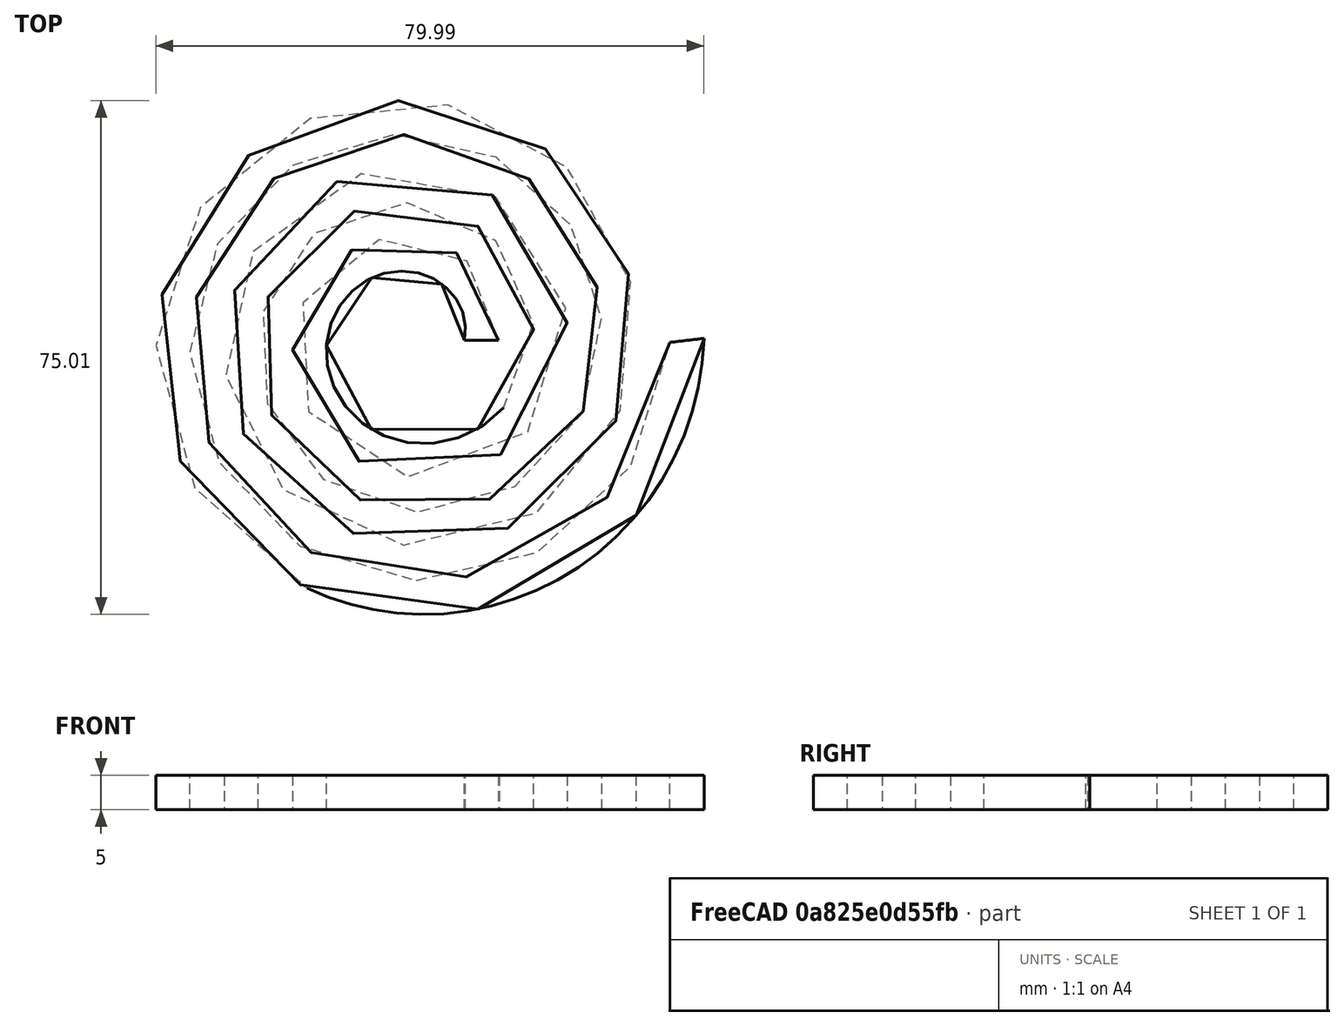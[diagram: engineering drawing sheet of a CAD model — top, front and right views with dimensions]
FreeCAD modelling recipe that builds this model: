
FCSTD DOCUMENT  (FreeCAD 0.16R6707 (Git))
Label: espiral-solida
License: All rights reserved
LicenseURL: http://en.wikipedia.org/wiki/All_rights_reserved
objects: Part::Spiral×1, Sketcher::SketchObject×1, Part::Sweep×1
note: 3 computed .brp shape members not serialized (recipe doc carries the construction recipe); baked Part::Feature solids carry a one-line shape summary decoded from their .brp

FEATURE [Part::Spiral] Spiral001  label="Espiral001"
  Growth = 10
  Radius = 10
  Rotations = 3
FEATURE [Sketcher::SketchObject] Sketch
  Placement = pos=(0,0,0) rot=(-1,0,0;4.71239rad)
  sketch-geometry (5):
    g0: LineSegment StartX=7.5 StartY=2.5 StartZ=0 EndX=12.5 EndY=2.5 EndZ=0
    g1: LineSegment StartX=12.5 StartY=2.5 StartZ=0 EndX=12.5 EndY=-2.5 EndZ=0
    g2: LineSegment StartX=12.5 StartY=-2.5 StartZ=0 EndX=7.5 EndY=-2.5 EndZ=0
    g3: LineSegment StartX=7.5 StartY=-2.5 StartZ=0 EndX=7.5 EndY=2.5 EndZ=0
    g4: LineSegment [constr] StartX=10 StartY=2.5 StartZ=0 EndX=10 EndY=-2.5 EndZ=0
  constraints (16):
    c: Coincident(g0,g1)
    c: Coincident(g1,g2)
    c: Coincident(g2,g3)
    c: Coincident(g3,g0)
    c: Horizontal(g0)
    c: Horizontal(g2)
    c: Vertical(g1)
    c: Vertical(g3)
    c: Equal(g0,g1)
    c: DistanceX(g0,g0) = 5
    c: Symmetric(g0,g2,g-1)
    c: Vertical(g4)
    c: PointOnObject(g4,g0)
    c: PointOnObject(g4,g2)
    c: Symmetric(g0,g0,g4)
    c: DistanceX(g-1,g4) = 10
FEATURE [Part::Sweep] Sweep
  Frenet = false
  Sections = -> [Sketch]
  Solid = true
  Spine = -> Spiral001 [Edge1]
  Transition = 1
